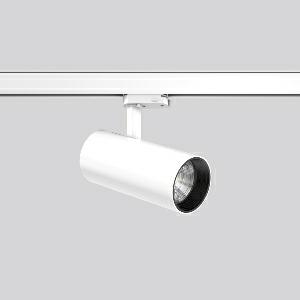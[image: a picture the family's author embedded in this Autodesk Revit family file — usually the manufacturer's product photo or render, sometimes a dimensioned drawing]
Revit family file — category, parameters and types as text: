
# Revit family: deecos_s_mini_742201_002_3_76_08d4
name_source: partatom
category: Lighting Fixtures
units: mm (PartAtom-declared; Revit-internal decimal feet)

## family parameters
Cut with Voids When Loaded = No
Host = Face
Light Source = No
Part Type = Normal
Room Calculation Point = No
Round Connector Dimension = Use Diameter
Shared = No

## types (1)
- DEECOS S mini (1 x LED Modul 935, 2300 lm, 3500)
    Apparent Load = 20 VA
    Approval mark = CE
    CIE Flux Codes = 80 99 100 100 100
    Color Rendering = 92
    Color Temperature = 3500
    Default Elevation = 1800 mm
    Description = Series: DEECOS S mini
LED surface-mounted projector in modern design with no visible cooling ribs. Housing: die-cast aluminium, powder-coated. Rotation range: 356°. Swivel range: 90°. Black plastic ring and recessed LED to prevent glare from the side. Optical assembly with lens made of plastic (polycarbonate) for the best homogeneous light distribution - can be changed without tools. Best colour rendering index Ra>90. With adapter for RZB 3-circuit DALI tracks. Suitable for Track on ceiling, Wall track. High quality converter without flickering and stroboscopic effect. The following accessories can be mounted without use of tools: interchangeable lenses, decorative glasses, honeycomb louvre, clear and frosted diffusers, white interchangeable plastic ring. 
Colour: traffic white, matt (RAL 9016)
Diameter: 87 mm
Height: 214 mm
Lamp: LED
Socket: without socket
Colour temperature: 3500K
Colour rendering index (CRI): 92
System power: 20 W
Rated luminous flux: 2300 lm
Luminous efficiency: 115 lm/W
Control gear: Converter, dimmable, DALI
Protection class: I
Type of protection: IP 20
    Height = 214 mm
    Lamp = 1 x LED Modul 935
    Lamp Light Flux = 2300 lm
    Lamp count = 1
    Length = 87 mm
    Lifetime = 50000 h
    Luminous efficacy = 115 lm/W
    Manufacturer = RZB
    ModVariant = No
    Model = 742201.002.3.76
    Mounting Place = Ceiling
    Mounting Type = Rail mounted
    Number of Poles = 1
    OnlyDefault = Yes
    Power Factor = 1
    Product Name = DEECOS S mini
    Product group = Track mounted projectors
    ProductGroupID = 301
    Protection Class = Protection class I
    Protection Degree = IP 20
    RLX_Detail_Level = 1
    RLX_Emergency_Light_Flux = 0 lm
    RLX_Emergency_Type = 0
    RLX_Emergency_Type_DB = No
    RlxData = <blob elided: 35381 chars, md5=c1f3b3a7>
    Socket = socket
    Standby Power = 0 W
    System Light Flux = 2300 lm
    System Power = 20 W
    Type Comments = Product without accessories
    Type Image = 741930.002.jpg
    URL = http://relux.com
    VarID = ---
    Voltage = 230 V
    Voltage Range = 220-240 V
    Weight = 0.00 kg
    Width = 0 mm  [stored 0 ft]

note: [stored X ft] marks values corroborated as IEEE doubles in the binary element streams (Revit-internal decimal feet)

## geometry (parser evidence)
native form markers: Blend x4, Sweep x13
no freeform markers — native parametric forms only
